FCSTD DOCUMENT  (FreeCAD 0.18R16161 (Git))
Label: fixator01_new1
License: All rights reserved
LicenseURL: http://en.wikipedia.org/wiki/All_rights_reserved
objects: Sketcher::SketchObject×1
note: 1 computed .brp shape members not serialized (recipe doc carries the construction recipe); baked Part::Feature solids carry a one-line shape summary decoded from their .brp

FEATURE [Sketcher::SketchObject] Sketch
  sketch-geometry (22):
    g0: LineSegment StartX=0 StartY=-2.88675 StartZ=0 EndX=2.5 EndY=1.44338 EndZ=0
    g1: LineSegment StartX=2.5 StartY=1.44338 StartZ=0 EndX=-2.5 EndY=1.44338 EndZ=0
    g2: LineSegment StartX=-2.5 StartY=1.44338 StartZ=0 EndX=0 EndY=-2.88675 EndZ=0
    g3: Circle [constr] CenterX=0 CenterY=0 CenterZ=0 NormalX=0 NormalY=0 NormalZ=1 AngleXU=0 Radius=2.88675
    g4: LineSegment StartX=2.5 StartY=1.44338 StartZ=0 EndX=7.5 EndY=1.44338 EndZ=0
    g5: LineSegment StartX=-7.5 StartY=1.44338 StartZ=0 EndX=-2.5 EndY=1.44338 EndZ=0
    g6: LineSegment StartX=0 StartY=-2.88675 StartZ=0 EndX=7.5 EndY=-2.88675 EndZ=0
    g7: LineSegment StartX=-7.5 StartY=-2.88675 StartZ=0 EndX=0 EndY=-2.88675 EndZ=0
    g8: LineSegment StartX=7.5 StartY=1.44338 StartZ=0 EndX=7.5 EndY=-2.88675 EndZ=0
    g9: LineSegment StartX=-7.5 StartY=1.44338 StartZ=0 EndX=-7.5 EndY=-2.88675 EndZ=0
    g10: LineSegment StartX=7.5 StartY=1.44338 StartZ=0 EndX=8.5 EndY=1.44338 EndZ=0
    g11: LineSegment StartX=8.5 StartY=1.44338 StartZ=0 EndX=8.5 EndY=-2.88675 EndZ=0
    g12: LineSegment StartX=8.5 StartY=-2.88675 StartZ=0 EndX=7.5 EndY=-2.88675 EndZ=0
    g13: LineSegment StartX=7.5 StartY=-2.88675 StartZ=0 EndX=7.5 EndY=1.44338 EndZ=0
    g14: LineSegment StartX=-8.5 StartY=1.44338 StartZ=0 EndX=-7.5 EndY=1.44338 EndZ=0
    g15: LineSegment StartX=-7.5 StartY=1.44338 StartZ=0 EndX=-7.5 EndY=-2.88675 EndZ=0
    g16: LineSegment StartX=-7.5 StartY=-2.88675 StartZ=0 EndX=-8.5 EndY=-2.88675 EndZ=0
    g17: LineSegment StartX=-8.5 StartY=-2.88675 StartZ=0 EndX=-8.5 EndY=1.44338 EndZ=0
    g18: LineSegment StartX=8.5 StartY=1.44338 StartZ=0 EndX=11 EndY=1.44338 EndZ=0
    g19: LineSegment StartX=8.5 StartY=-2.88675 StartZ=0 EndX=11 EndY=1.44338 EndZ=0
    g20: LineSegment StartX=-11 StartY=1.44338 StartZ=0 EndX=-8.5 EndY=1.44338 EndZ=0
    g21: LineSegment StartX=-11 StartY=1.44338 StartZ=0 EndX=-8.5 EndY=-2.88675 EndZ=0
  constraints (59):
    c: Coincident(g0,g1)
    c: Coincident(g1,g2)
    c: Coincident(g2,g0)
    c: Equal(g0,g1)
    c: Equal(g0,g2)
    c: PointOnObject(g0,g3)
    c: PointOnObject(g1,g3)
    c: PointOnObject(g2,g3)
    c: Coincident(g3,g-1)
    c: PointOnObject(g0,g-2)
    c: DistanceX(g1,g1) = 5
    c: Coincident(g4,g0)
    c: Coincident(g5,g1)
    c: Horizontal(g4)
    c: Horizontal(g5)
    c: Equal(g4,g5)
    c: DistanceX(g4,g4) = 5
    c: Coincident(g7,g0)
    c: Coincident(g6,g0)
    c: Horizontal(g6)
    c: Horizontal(g7)
    c: Coincident(g9,g5)
    c: Coincident(g8,g4)
    c: Vertical(g8)
    c: Vertical(g9)
    c: Coincident(g7,g9)
    c: Coincident(g6,g8)
    c: Coincident(g10,g11)
    c: Coincident(g11,g12)
    c: Coincident(g12,g13)
    c: Coincident(g13,g10)
    c: Horizontal(g10)
    c: Horizontal(g12)
    c: Vertical(g11)
    c: Vertical(g13)
    c: Coincident(g14,g15)
    c: Coincident(g15,g16)
    c: Coincident(g16,g17)
    c: Coincident(g17,g14)
    c: Horizontal(g14)
    c: Horizontal(g16)
    c: Vertical(g15)
    c: Vertical(g17)
    c: Coincident(g10,g4)
    c: Equal(g11,g8)
    c: DistanceX(g10,g10) = 1
    c: Coincident(g14,g5)
    c: Equal(g17,g9)
    c: Equal(g14,g10)
    c: Coincident(g18,g10)
    c: Coincident(g19,g11)
    c: Coincident(g19,g18)
    c: Horizontal(g18)
    c: Angle(g19,g11) = 0.523599
    c: Coincident(g20,g21)
    c: Coincident(g20,g14)
    c: Coincident(g21,g16)
    c: Horizontal(g20)
    c: Equal(g18,g20)
